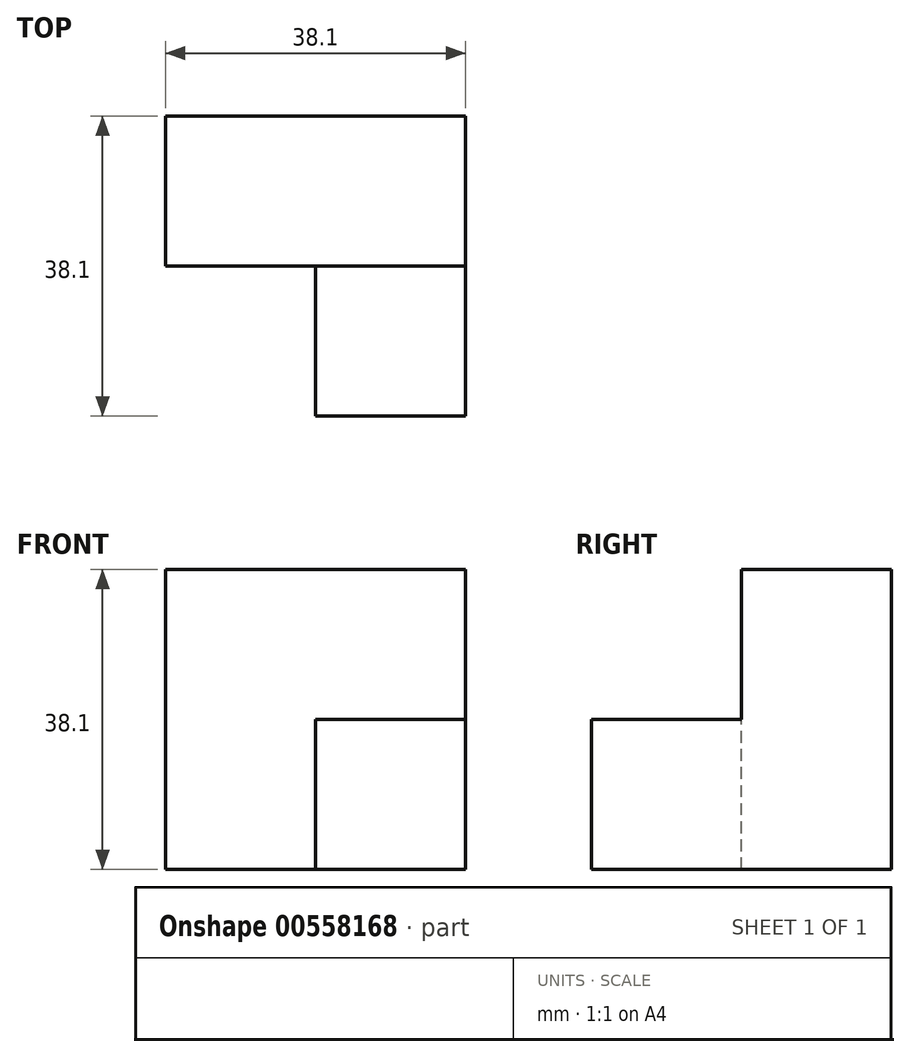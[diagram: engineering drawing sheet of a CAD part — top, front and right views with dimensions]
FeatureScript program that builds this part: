
annotation { "Feature Type Name" : "Feature", "Feature Type Description" : "" }
export const myFeature = defineFeature(function(context is Context, id is Id, definition is map)
    precondition{}
    {
        {
            var Q0;
            Q0=qCreatedBy(makeId("Front.planeOp"),FACE);
            var sketch = newSketch(context, id + "F0", { "sketchPlane" : qUnion([Q0])});
            skLineSegment(sketch, "E0", {"start": v(0, 0) * mm, "end": v(-38.1, 0) * mm});
            skLineSegment(sketch, "E1", {"start": v(-38.1, 0) * mm, "end": v(-38.1, 38.1) * mm});
            skLineSegment(sketch, "E2", {"start": v(-38.1, 38.1) * mm, "end": v(0, 38.1) * mm});
            skLineSegment(sketch, "E3", {"start": v(0, 38.1) * mm, "end": v(0, 0) * mm});
            skSolve(sketch);
        }
        {
            var Q0;
            Q0 = qSketchRegion(id + "F0", true);
            extrude(context, id + "F1", {"entities" : qUnion([Q0]), "depth" : 19.05 * mm, "offsetDistance" : 25.4 * mm});
        }
        {
            var Q0;
            Q0=makeQuery(id+"F1.opExtrude","CAP_FACE",FACE,{"disambiguationData":[OSD([sQuery(id+"F0.wireOp",EDGE,"E0"),sQuery(id+"F0.wireOp",EDGE,"E1"),sQuery(id+"F0.wireOp",EDGE,"E2"),sQuery(id+"F0.wireOp",EDGE,"E3")])],"isStart":false});
            var sketch = newSketch(context, id + "F2", { "sketchPlane" : qUnion([Q0])});
            skLineSegment(sketch, "E4", {"start": v(0, 0) * mm, "end": v(-19.05, 0) * mm});
            skLineSegment(sketch, "E5", {"start": v(-19.05, 0) * mm, "end": v(-19.05, 19.05) * mm});
            skLineSegment(sketch, "E6", {"start": v(-19.05, 19.05) * mm, "end": v(0, 19.05) * mm});
            skLineSegment(sketch, "E7", {"start": v(0, 19.05) * mm, "end": v(0, 0) * mm});
            skSolve(sketch);
        }
        {
            var Q0;
            Q0 = qSketchRegion(id + "F2", true);
            extrude(context, id + "F3", {"entities" : qUnion([Q0]), "operationType" : NewBodyOperationType.ADD, "depth" : 19.05 * mm, "offsetDistance" : 25.4 * mm});
        }
    });
